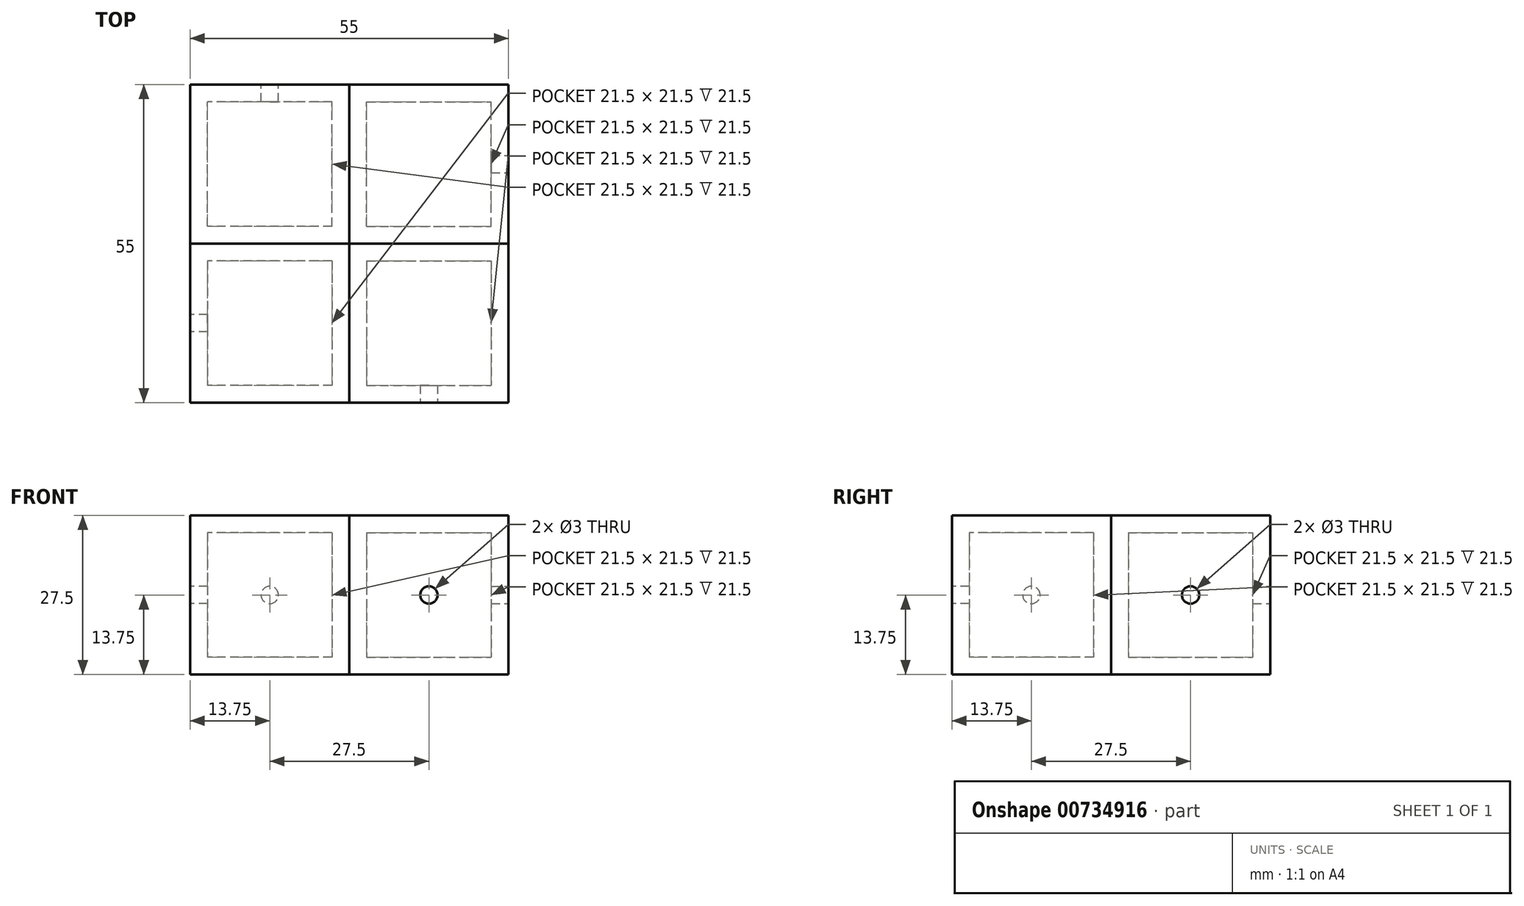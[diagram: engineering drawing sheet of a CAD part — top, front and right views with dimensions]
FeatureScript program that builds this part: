
annotation { "Feature Type Name" : "Feature", "Feature Type Description" : "" }
export const myFeature = defineFeature(function(context is Context, id is Id, definition is map)
    precondition{}
    {
        {
            var Q0;
            Q0=qCreatedBy(makeId("Top.planeOp"),FACE);
            var sketch = newSketch(context, id + "F0", { "sketchPlane" : qUnion([Q0])});
            skLineSegment(sketch, "E0.bottom", {"start": v(0, 0) * mm, "end": v(-27.5, 0) * mm});
            skLineSegment(sketch, "E0.top", {"start": v(0, 27.5) * mm, "end": v(-27.5, 27.5) * mm});
            skLineSegment(sketch, "E0.left", {"start": v(0, 0) * mm, "end": v(0, 27.5) * mm});
            skLineSegment(sketch, "E0.right", {"start": v(-27.5, 0) * mm, "end": v(-27.5, 27.5) * mm});
            skSolve(sketch);
        }
        {
            var Q0;
            Q0=makeQuery(id+"F0.imprint","IMPRINT",FACE,{"disambiguationData":[TD([[makeQuery(id+"F0.imprint","IMPRINT",EDGE,{"derivedFrom":sQuery(id+"F0.wireOp",EDGE,"E0.bottom")}),-1.0]])]});
            extrude(context, id + "F1", {"entities" : qUnion([Q0]), "depth" : 27.5 * mm, "offsetDistance" : 25 * mm});
        }
        {
            var Q0;
            Q0=qCreatedBy(makeId("Top.planeOp"),FACE);
            var sketch = newSketch(context, id + "F2", { "sketchPlane" : qUnion([Q0])});
            skLineSegment(sketch, "E1.bottom", {"start": v(-24.5, 24.5) * mm, "end": v(-3, 24.5) * mm});
            skLineSegment(sketch, "E1.top", {"start": v(-24.5, 3) * mm, "end": v(-3, 3) * mm});
            skLineSegment(sketch, "E1.left", {"start": v(-24.5, 24.5) * mm, "end": v(-24.5, 3) * mm});
            skLineSegment(sketch, "E1.right", {"start": v(-3, 24.5) * mm, "end": v(-3, 3) * mm});
            skSolve(sketch);
        }
        {
            var Q0;
            Q0=qCreatedBy(makeId("Top.planeOp"),FACE);
            cPlane(context, id + "F3", {"entities" : qUnion([Q0]), "cplaneType" : CPlaneType.OFFSET, "offset" : 3 * mm, "width" : 150 * mm, "height" : 150 * mm});
        }
        {
            var Q0;
            Q0=qCreatedBy(id+"F3.planeOp",FACE);
            var sketch = newSketch(context, id + "F4", { "sketchPlane" : qUnion([Q0])});
            skLineSegment(sketch, "E2.bottom", {"start": v(-3, 3) * mm, "end": v(-24.5, 3) * mm});
            skLineSegment(sketch, "E2.top", {"start": v(-3, 24.5) * mm, "end": v(-24.5, 24.5) * mm});
            skLineSegment(sketch, "E2.left", {"start": v(-3, 3) * mm, "end": v(-3, 24.5) * mm});
            skLineSegment(sketch, "E2.right", {"start": v(-24.5, 3) * mm, "end": v(-24.5, 24.5) * mm});
            skSolve(sketch);
        }
        {
            var Q0;
            Q0 = qSketchRegion(id + "F4", true);
            extrude(context, id + "F5", {"entities" : qUnion([Q0]), "operationType" : NewBodyOperationType.REMOVE, "depth" : 21.5 * mm, "offsetDistance" : 25 * mm});
        }
        {
            var Q0;
            Q0=makeQuery(id+"F1.opExtrude","SWEPT_FACE",FACE,{"disambiguationData":[OSD([sQuery(id+"F0.wireOp",EDGE,"E0.left")])]});
            var sketch = newSketch(context, id + "F6", { "sketchPlane" : qUnion([Q0])});
            skCircle(sketch, "E3", {"center": v(13.75, 13.75) * mm, "radius": 1.5 * mm});
            skSolve(sketch);
        }
        {
            var Q0;
            Q0=makeQuery(id+"F1.opExtrude","SWEPT_FACE",FACE,{"disambiguationData":[OSD([sQuery(id+"F0.wireOp",EDGE,"E0.top")])]});
            var sketch = newSketch(context, id + "F7", { "sketchPlane" : qUnion([Q0])});
            skCircle(sketch, "E4", {"center": v(13.75, 13.75) * mm, "radius": 1.5 * mm});
            skSolve(sketch);
        }
        {
            var Q0;
            Q0=makeQuery(id+"F7.imprint","IMPRINT",FACE,{"disambiguationData":[TD([[makeQuery(id+"F7.imprint","IMPRINT",EDGE,{"derivedFrom":sQuery(id+"F7.wireOp",EDGE,"E4")}),1.0]])]});
            var Q1;
            Q1=sQuery(id+"F7.wireOp",EDGE,"E4");
            extrude(context, id + "F8", {"entities" : qUnion([Q0]), "operationType" : NewBodyOperationType.REMOVE, "surfaceEntities" : qUnion([Q1]), "oppositeDirection" : true, "depth" : 5 * mm, "offsetDistance" : 25 * mm});
        }
        {
            var Q0;
            Q0=makeQuery(id+"F1.opExtrude","SWEPT_BODY",BODY,{"disambiguationData":[OSD([sQuery(id+"F0.wireOp",EDGE,"E0.bottom"),sQuery(id+"F0.wireOp",EDGE,"E0.top"),sQuery(id+"F0.wireOp",EDGE,"E0.left"),sQuery(id+"F0.wireOp",EDGE,"E0.right")])]});
            var Q1;
            Q1=makeQuery(id+"F1.opExtrude","SWEPT_EDGE",EDGE,{"disambiguationData":[OSD([sQuery(id+"F0.wireOp",EDGE,"E0.bottom"),sQuery(id+"F0.wireOp",EDGE,"E0.left")])]});
            circularPattern(context, id + "F9", {"entities" : qUnion([Q0]), "axis" : qUnion([Q1]), "angle" : 360 * degree, "instanceCount" : 4, "equalSpace" : true});
        }
    });
